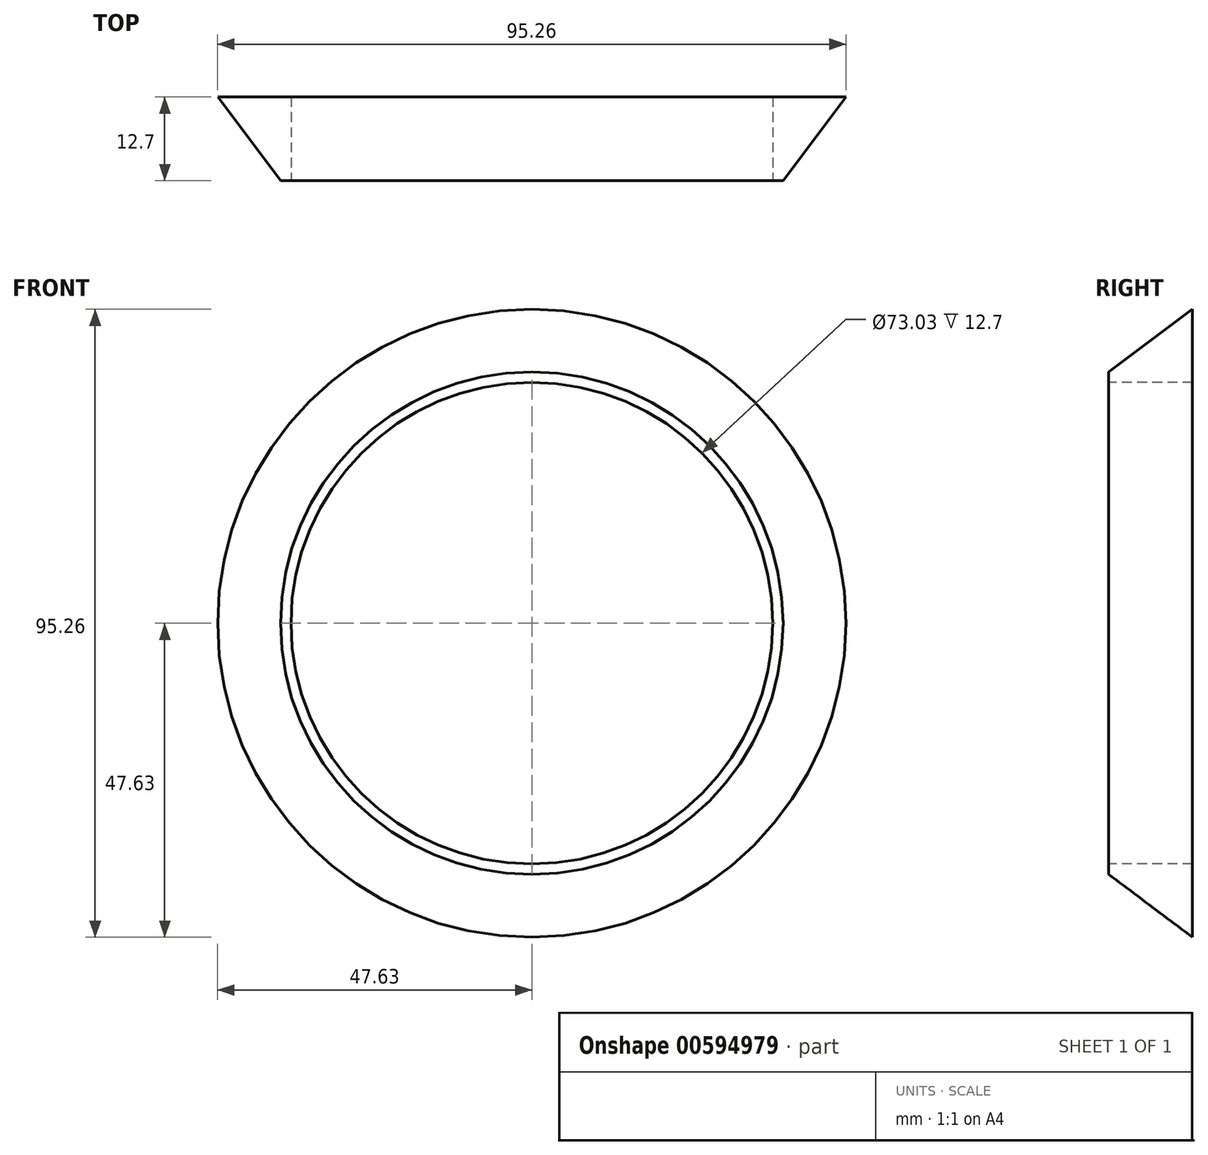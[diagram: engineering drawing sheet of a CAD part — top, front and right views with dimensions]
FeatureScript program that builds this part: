
annotation { "Feature Type Name" : "Feature", "Feature Type Description" : "" }
export const myFeature = defineFeature(function(context is Context, id is Id, definition is map)
    precondition{}
    {
        {
            var Q0;
            Q0=qCreatedBy(makeId("Front.planeOp"),FACE);
            var sketch = newSketch(context, id + "F0", { "sketchPlane" : qUnion([Q0])});
            skCircle(sketch, "E0", {"center": v(0, 0) * mm, "radius": 38.1 * mm});
            skSolve(sketch);
        }
        {
            var Q0;
            Q0=qCreatedBy(makeId("Front.planeOp"),FACE);
            cPlane(context, id + "F1", {"entities" : qUnion([Q0]), "cplaneType" : CPlaneType.OFFSET, "offset" : 12.7 * mm, "oppositeDirection" : true, "width" : 152.4 * mm, "height" : 152.4 * mm});
        }
        {
            var Q0;
            Q0=qCreatedBy(id+"F1.planeOp",FACE);
            var sketch = newSketch(context, id + "F2", { "sketchPlane" : qUnion([Q0])});
            skCircle(sketch, "E1", {"center": v(0, 0) * mm, "radius": 47.63 * mm});
            skSolve(sketch);
        }
        {
            var Q0;
            Q0=makeQuery(id+"F0.imprint","IMPRINT",FACE,{"disambiguationData":[TD([[makeQuery(id+"F0.imprint","IMPRINT",EDGE,{"derivedFrom":sQuery(id+"F0.wireOp",EDGE,"E0")}),1.0]])]});
            var Q1;
            Q1=makeQuery(id+"F2.imprint","IMPRINT",FACE,{"disambiguationData":[TD([[makeQuery(id+"F2.imprint","IMPRINT",EDGE,{"derivedFrom":sQuery(id+"F2.wireOp",EDGE,"E1")}),1.0]])]});
            loft(context, id + "F3", {"sheetProfilesArray" : [{ "sheetProfileEntities" : qUnion([Q0]) }, { "sheetProfileEntities" : qUnion([Q1]) }]});
        }
        {
            var Q0;
            Q0=qCreatedBy(makeId("Front.planeOp"),FACE);
            var sketch = newSketch(context, id + "F4", { "sketchPlane" : qUnion([Q0])});
            skCircle(sketch, "E2", {"center": v(0, 0) * mm, "radius": 36.51 * mm});
            skSolve(sketch);
        }
        {
            var Q0;
            Q0=qSketchRegion(id+"F4",true);
            extrude(context, id + "F5", {"entities" : qUnion([Q0]), "operationType" : NewBodyOperationType.REMOVE, "oppositeDirection" : true, "depth" : 25.4 * mm, "offsetDistance" : 25.4 * mm});
        }
    });
